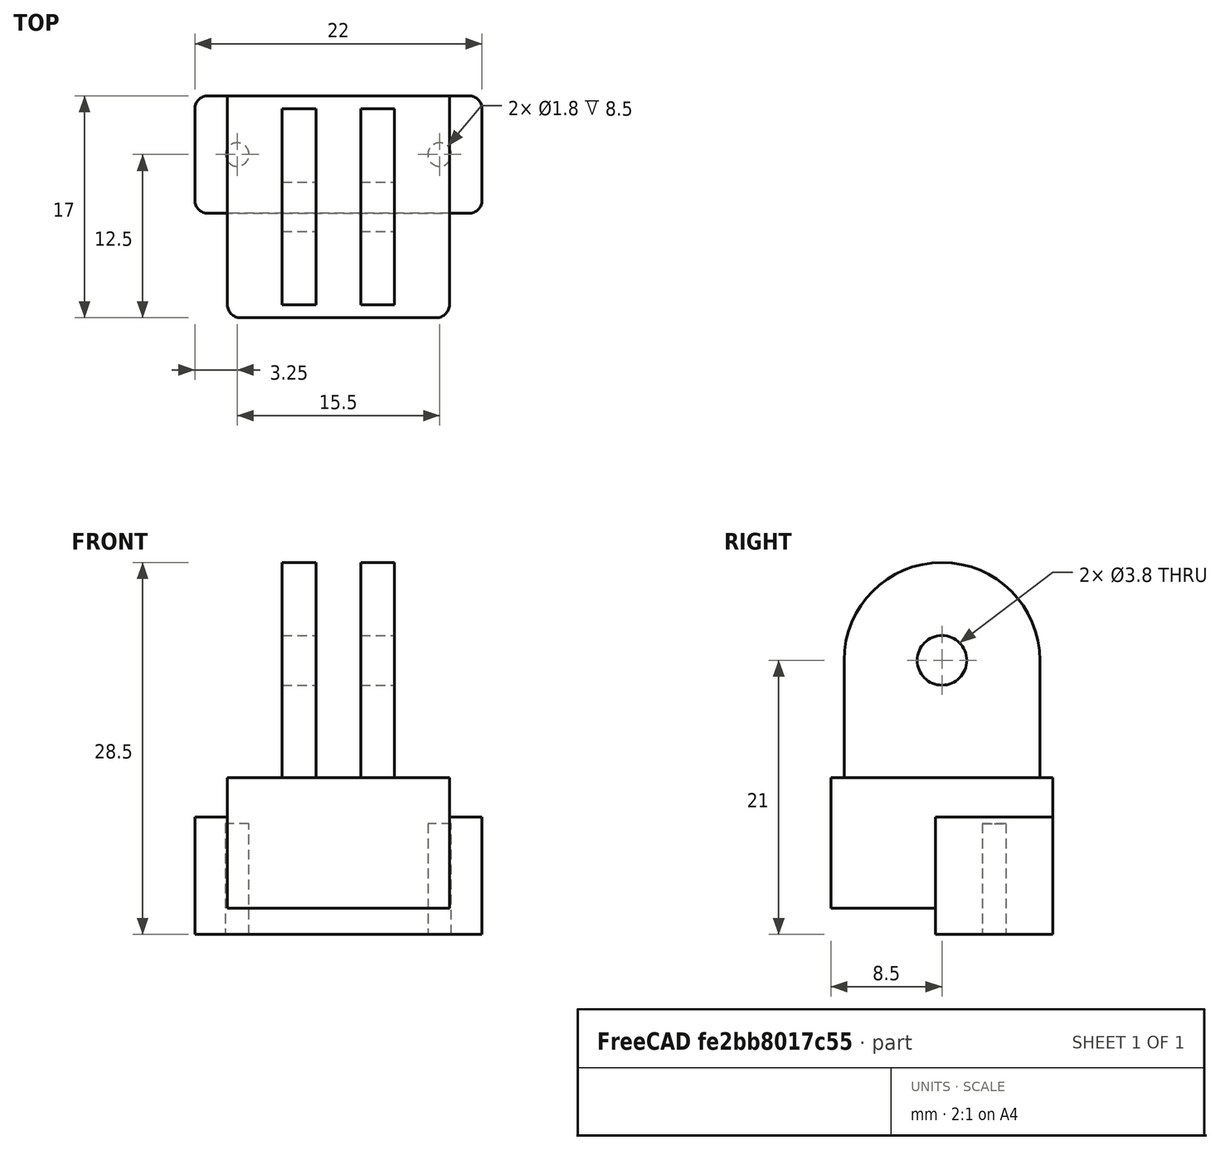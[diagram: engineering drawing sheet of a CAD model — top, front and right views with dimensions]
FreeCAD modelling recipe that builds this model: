
FCSTD DOCUMENT  (FreeCAD 0.20R29410 (Git))
Label: hmc5883l+Accel+gyro+pressure
License: FreeArt
LicenseURL: http://artlibre.org/licence/lal
objects: Part::Box×2, Spreadsheet::Sheet×1, Part::Cylinder×1, Part::FeaturePython×1, Part::Feature×1, Part::MultiFuse×1, Part::Cut×1, Part::Fillet×1, App::Part×1
note: 8 computed .brp shape members not serialized (recipe doc carries the construction recipe); baked Part::Feature solids carry a one-line shape summary decoded from their .brp

FEATURE [Spreadsheet::Sheet] Spreadsheet  label="p"
  cells = A1=pcb_x; B1(pcb_x)==22mm; A2=pcb_y; B2(pcb_y)==9mm; A3=pcb_z; B3(pcb_z)==1.7mm; A4=hole_dist_x; B4(hole_dist_x)==15.5mm; A5=hole_offset_y; B5(hole_offset_y)==pcb_y / 2; A6=hole_r; B6(hole_r)==0.9mm; A7=stick_width; B7(stick_width)==17mm; A8=stick_length; B8(stick_length)==10mm; A9=pcb_wall; B9(pcb_wall)==9mm; A10=pcb_back; B10(pcb_back)==6.5mm
FEATURE [Part::Cylinder] Cylinder  label="bolt hole"
  Angle = 360
  AttacherType = Attacher::AttachEngine3D
  FirstAngle = 0
  Height = 15
  Radius = 0.9
  SecondAngle = 0
  expr: Radius = <<p>>.hole_r
FEATURE [Part::FeaturePython] Array  label="bolt hole array"  # Draft array (typed FeaturePython)
  Angle = 360
  ArrayType = 0
  Axis = (0,0,1)
  Base = -> Cylinder
  Center = (0,0,0)
  Fuse = false
  IntervalAxis = (0,0,0)
  IntervalX = (15.5,0,0)
  IntervalY = (0,1,0)
  IntervalZ = (0,0,1)
  NumberPolar = 1
  NumberX = 2
  NumberY = 1
  NumberZ = 1
  Placement = pos=(0.75,12.5,-2) rot=(0,0,1;0rad)
  expr: .IntervalX.x = <<p>>.hole_dist_x
  expr: .Placement.Base.x = (<<p>>.stick_width - <<p>>.hole_dist_x) / 2
  expr: .Placement.Base.y = <<p>>.stick_width - <<p>>.pcb_y + <<p>>.hole_offset_y
FEATURE [Part::Box] Box002  label="stick cube"
  AttacherType = Attacher::AttachEngine3D
  Height = 10
  Length = 17
  Placement = pos=(0,0,6.5) rot=(0,0,1;0rad)
  Width = 17
  expr: .Placement.Base.z = <<p>>.pcb_back
  expr: Height = <<p>>.stick_length
  expr: Length = <<p>>.stick_width
  expr: Width = <<p>>.stick_width
FEATURE [Part::Feature] Cut001001  label="side 2 cut001"
  Placement = pos=(8.5,8.5,13) rot=(0,0,1;1.5708rad)
  shape: bbox 15 x 15 x 20 mm, 16 faces (baked)
  expr: .Placement.Base.x = <<p>>.stick_width / 2
  expr: .Placement.Base.y = <<p>>.stick_width / 2
  expr: .Placement.Base.z = <<p>>.stick_length + 3mm
FEATURE [Part::Box] Box003  label="pcb wall"
  AttacherType = Attacher::AttachEngine3D
  Height = 9
  Length = 22
  Placement = pos=(-2.5,8,4.5) rot=(0,0,1;0rad)
  Width = 9
  expr: .Placement.Base.x = -(<<p>>.pcb_x - <<p>>.stick_width) / 2
  expr: .Placement.Base.y = <<p>>.stick_width - <<p>>.pcb_y
  expr: .Placement.Base.z = <<p>>.pcb_wall / 2
  expr: Height = <<p>>.pcb_wall
  expr: Length = <<p>>.pcb_x
  expr: Width = <<p>>.pcb_y
FEATURE [Part::MultiFuse] Fusion  label="holder fusion"
  Shapes = -> [Box002,Cut001001,Box003]
FEATURE [Part::Cut] Cut  label="sensor cut"
  Base = -> Fusion
  Tool = -> Array
FEATURE [Part::Fillet] Fillet  label="sensor fillet"
  Base = -> Cut
  Edges = 6 edges r=1: [Edge6,Edge23,Edge27,Edge31,Edge60,Edge62]
FEATURE [App::Part] Part  label="hmc5883l sensor part"
  Group = -> [Fillet]
  Origin = -> Origin
